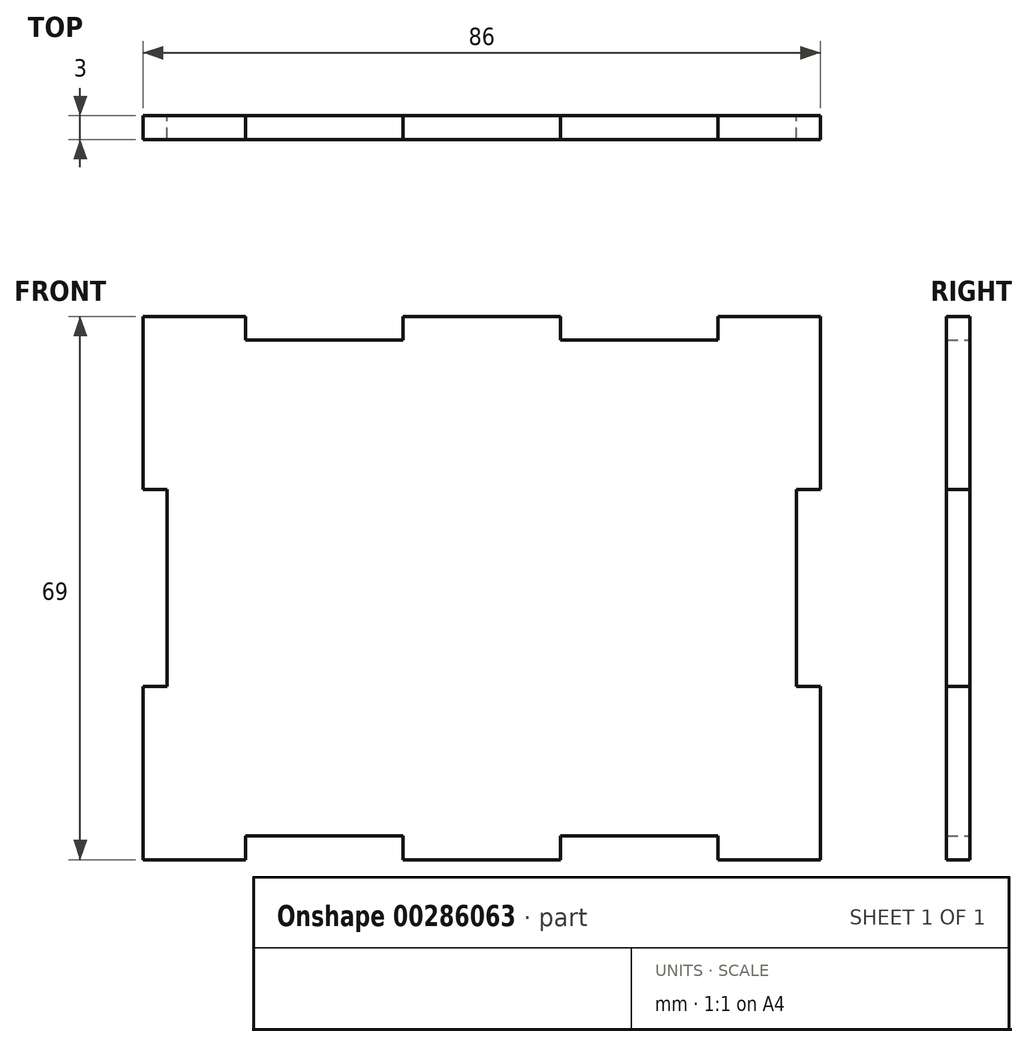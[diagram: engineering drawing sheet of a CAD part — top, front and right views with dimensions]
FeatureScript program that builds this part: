
annotation { "Feature Type Name" : "Feature", "Feature Type Description" : "" }
export const myFeature = defineFeature(function(context is Context, id is Id, definition is map)
    precondition{}
    {
        {
            var Q0;
            Q0=qCreatedBy(makeId("Front.planeOp"),FACE);
            var sketch = newSketch(context, id + "F0", { "sketchPlane" : qUnion([Q0])});
            skLineSegment(sketch, "E0.bottom", {"start": v(40, -34.5) * mm, "end": v(-40, -34.5) * mm, "construction": true});
            skLineSegment(sketch, "E0.top", {"start": v(40, 34.5) * mm, "end": v(-40, 34.5) * mm, "construction": true});
            skLineSegment(sketch, "E0.left", {"start": v(40, -34.5) * mm, "end": v(40, 34.5) * mm, "construction": true});
            skLineSegment(sketch, "E0.right", {"start": v(-40, -34.5) * mm, "end": v(-40, 34.5) * mm, "construction": true});
            skPoint(sketch, "E0.middle", {"position": v(0, 0) * mm});
            skLineSegment(sketch, "E1", {"start": v(0, 34.5) * mm, "end": v(-10, 34.5) * mm});
            skLineSegment(sketch, "E2", {"start": v(-10, 34.5) * mm, "end": v(-10, 31.5) * mm});
            skLineSegment(sketch, "E3", {"start": v(-10, 31.5) * mm, "end": v(-30, 31.5) * mm});
            skLineSegment(sketch, "E4", {"start": v(-30, 31.5) * mm, "end": v(-30, 34.5) * mm});
            skLineSegment(sketch, "E5", {"start": v(-30, 34.5) * mm, "end": v(-43, 34.5) * mm});
            skLineSegment(sketch, "E6", {"start": v(-43, 34.5) * mm, "end": v(-43, 12.5) * mm});
            skLineSegment(sketch, "E7", {"start": v(-43, 12.5) * mm, "end": v(-40, 12.5) * mm});
            skLineSegment(sketch, "E8", {"start": v(-40, 12.5) * mm, "end": v(-40, 0) * mm});
            skLineSegment(sketch, "E9.MirrorCS", {"start": v(40, 12.5) * mm, "end": v(40, 0) * mm});
            skLineSegment(sketch, "E10.MirrorCS", {"start": v(43, 12.5) * mm, "end": v(40, 12.5) * mm});
            skLineSegment(sketch, "E11.MirrorCS", {"start": v(43, 34.5) * mm, "end": v(43, 12.5) * mm});
            skLineSegment(sketch, "E12.MirrorCS", {"start": v(30, 34.5) * mm, "end": v(43, 34.5) * mm});
            skLineSegment(sketch, "E13.MirrorCS", {"start": v(30, 31.5) * mm, "end": v(30, 34.5) * mm});
            skLineSegment(sketch, "E14.MirrorCS", {"start": v(0, 34.5) * mm, "end": v(10, 34.5) * mm});
            skLineSegment(sketch, "E15.MirrorCS", {"start": v(10, 31.5) * mm, "end": v(30, 31.5) * mm});
            skLineSegment(sketch, "E16", {"start": v(10, 34.5) * mm, "end": v(10, 31.5) * mm});
            skLineSegment(sketch, "E17.MirrorCS", {"start": v(10, -31.5) * mm, "end": v(30, -31.5) * mm});
            skLineSegment(sketch, "E18.MirrorCS", {"start": v(-43, -12.5) * mm, "end": v(-40, -12.5) * mm});
            skLineSegment(sketch, "E19.MirrorCS", {"start": v(-30, -34.5) * mm, "end": v(-43, -34.5) * mm});
            skLineSegment(sketch, "E20.MirrorCS", {"start": v(-30, -31.5) * mm, "end": v(-30, -34.5) * mm});
            skLineSegment(sketch, "E21.MirrorCS", {"start": v(-10, -31.5) * mm, "end": v(-30, -31.5) * mm});
            skLineSegment(sketch, "E22.MirrorCS", {"start": v(0, -34.5) * mm, "end": v(-10, -34.5) * mm});
            skLineSegment(sketch, "E23.MirrorCS", {"start": v(0, -34.5) * mm, "end": v(10, -34.5) * mm});
            skLineSegment(sketch, "E24.MirrorCS", {"start": v(30, -34.5) * mm, "end": v(43, -34.5) * mm});
            skLineSegment(sketch, "E25.MirrorCS", {"start": v(43, -12.5) * mm, "end": v(40, -12.5) * mm});
            skLineSegment(sketch, "E26.MirrorCS", {"start": v(40, -12.5) * mm, "end": v(40, 0) * mm});
            skLineSegment(sketch, "E27.MirrorCS", {"start": v(43, -34.5) * mm, "end": v(43, -12.5) * mm});
            skLineSegment(sketch, "E28.MirrorCS", {"start": v(30, -31.5) * mm, "end": v(30, -34.5) * mm});
            skLineSegment(sketch, "E29.MirrorCS", {"start": v(10, -34.5) * mm, "end": v(10, -31.5) * mm});
            skLineSegment(sketch, "E30.MirrorCS", {"start": v(-10, -34.5) * mm, "end": v(-10, -31.5) * mm});
            skLineSegment(sketch, "E31.MirrorCS", {"start": v(-40, -12.5) * mm, "end": v(-40, 0) * mm});
            skLineSegment(sketch, "E32.MirrorCS", {"start": v(-43, -34.5) * mm, "end": v(-43, -12.5) * mm});
            skSolve(sketch);
        }
        {
            var Q0;
            Q0 = qSketchRegion(id + "F0", true);
            extrude(context, id + "F1", {"entities" : qUnion([Q0]), "depth" : 3 * mm});
        }
    });
